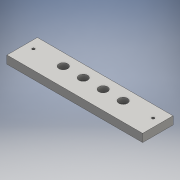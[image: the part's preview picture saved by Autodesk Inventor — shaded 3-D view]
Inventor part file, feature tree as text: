
AUTODESK INVENTOR PART (.ipt)
format: ipt  version: 2016 (Build 200138000, 138)  size: 121,856 bytes
history: native  units: mm
features: sketch x3, hole x2, extrude x1
ambient origin geometry x8: Origin, YZ Plane, XZ Plane, XY Plane, X Axis, Y Axis, Z Axis, Center Point
bodies: Solid1 (feature_tree)
feature tree (6):
  extrude  "Extrusion1"  Depth=170.0mm
  hole  "Hole1"  [1 undecoded]
  hole  "Hole2"  [1 undecoded]
  sketch  "Sketch1"  dims[d0=30.0mm d1=170.0mm]
  sketch  "Sketch2"  dims[d2=85.0mm d3=15.0mm]
  sketch  "Sketch3"  dims[d4=10.0mm d5=0.0mm d9=6.6mm d10=6.0mm d11=11.0mm d12=7.0mm d13=90.0deg d14=8.0mm d15=20.594885mm d16=150.0mm d17=75.0mm d19=3.242mm d20=8.0mm d21=19.05mm d22=4.775mm d23=90.0deg d24=11.8mm d25=20.594885mm d30=25.0mm d31=25.0mm d32=25.0mm d33=12.5mm d34=8.1mm d35=170.0mm]
note: 2 required parameter values undecoded (feature->parameter linkage not recoverable at this tier; creation-order binding heuristic only, values carry confidence <= 0.55)
